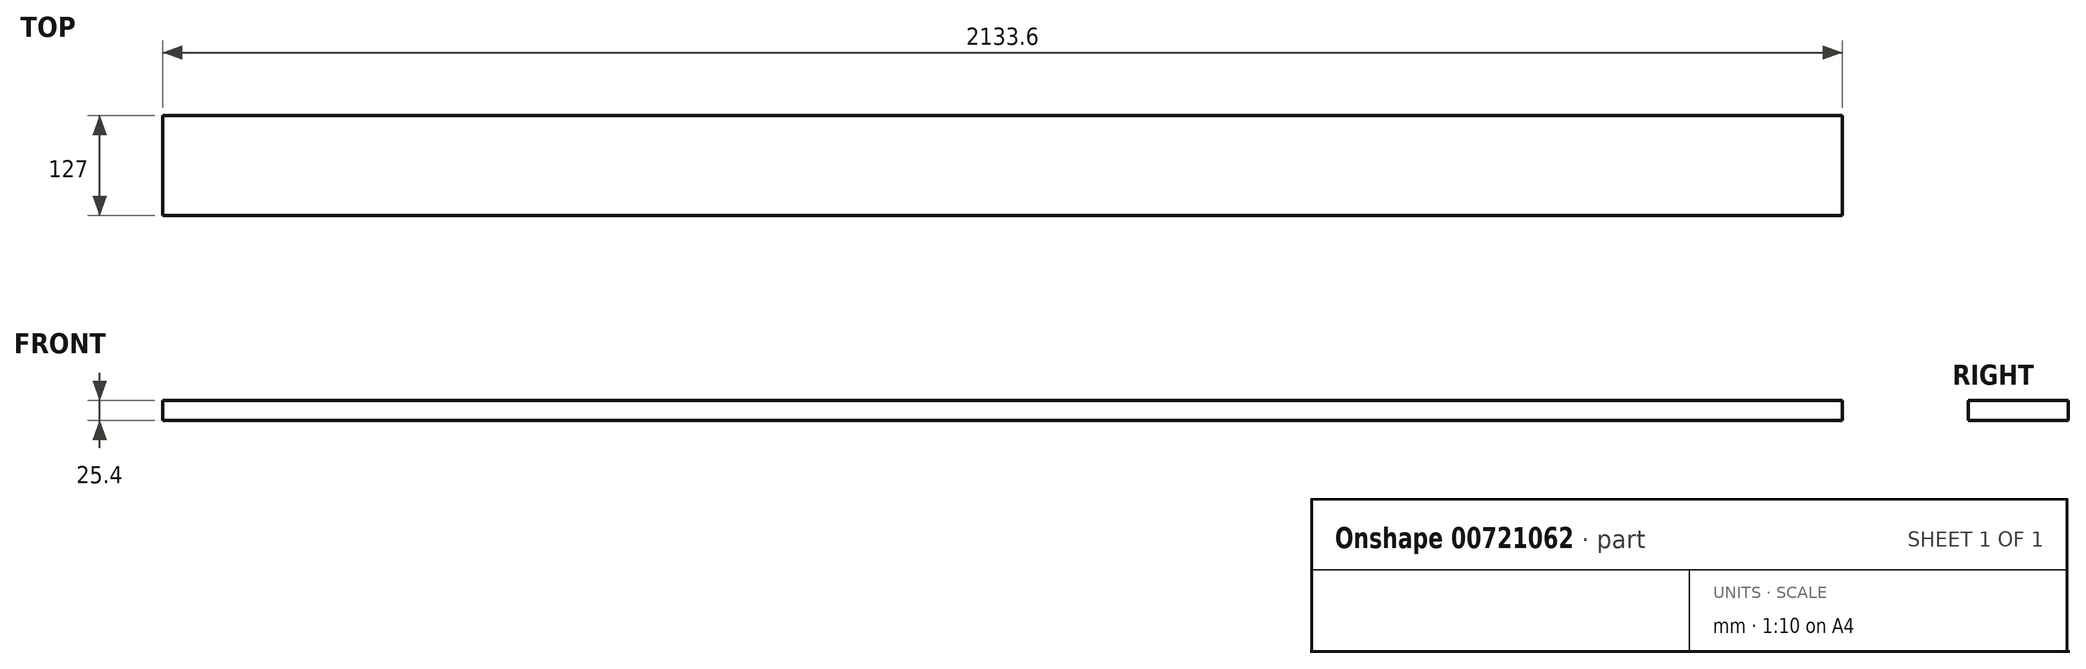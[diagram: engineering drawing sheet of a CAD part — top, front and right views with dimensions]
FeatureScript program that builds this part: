
annotation { "Feature Type Name" : "Feature", "Feature Type Description" : "" }
export const myFeature = defineFeature(function(context is Context, id is Id, definition is map)
    precondition{}
    {
        {
            var Q0;
            Q0=qCreatedBy(makeId("Top.planeOp"),FACE);
            var sketch = newSketch(context, id + "F0", { "sketchPlane" : qUnion([Q0])});
            skLineSegment(sketch, "E0.bottom", {"start": v(0, 0) * mm, "end": v(2133.6, 0) * mm});
            skLineSegment(sketch, "E0.top", {"start": v(0, 127) * mm, "end": v(2133.6, 127) * mm});
            skLineSegment(sketch, "E0.left", {"start": v(0, 0) * mm, "end": v(0, 127) * mm});
            skLineSegment(sketch, "E0.right", {"start": v(2133.6, 0) * mm, "end": v(2133.6, 127) * mm});
            skSolve(sketch);
        }
        {
            var Q0;
            Q0=makeQuery(id+"F0.imprint","IMPRINT",FACE,{"disambiguationData":[TD([[makeQuery(id+"F0.imprint","IMPRINT",EDGE,{"derivedFrom":sQuery(id+"F0.wireOp",EDGE,"E0.bottom")}),1.0]])]});
            extrude(context, id + "F1", {"entities" : qUnion([Q0]), "depth" : 25.4 * mm, "offsetDistance" : 25.4 * mm});
        }
    });
